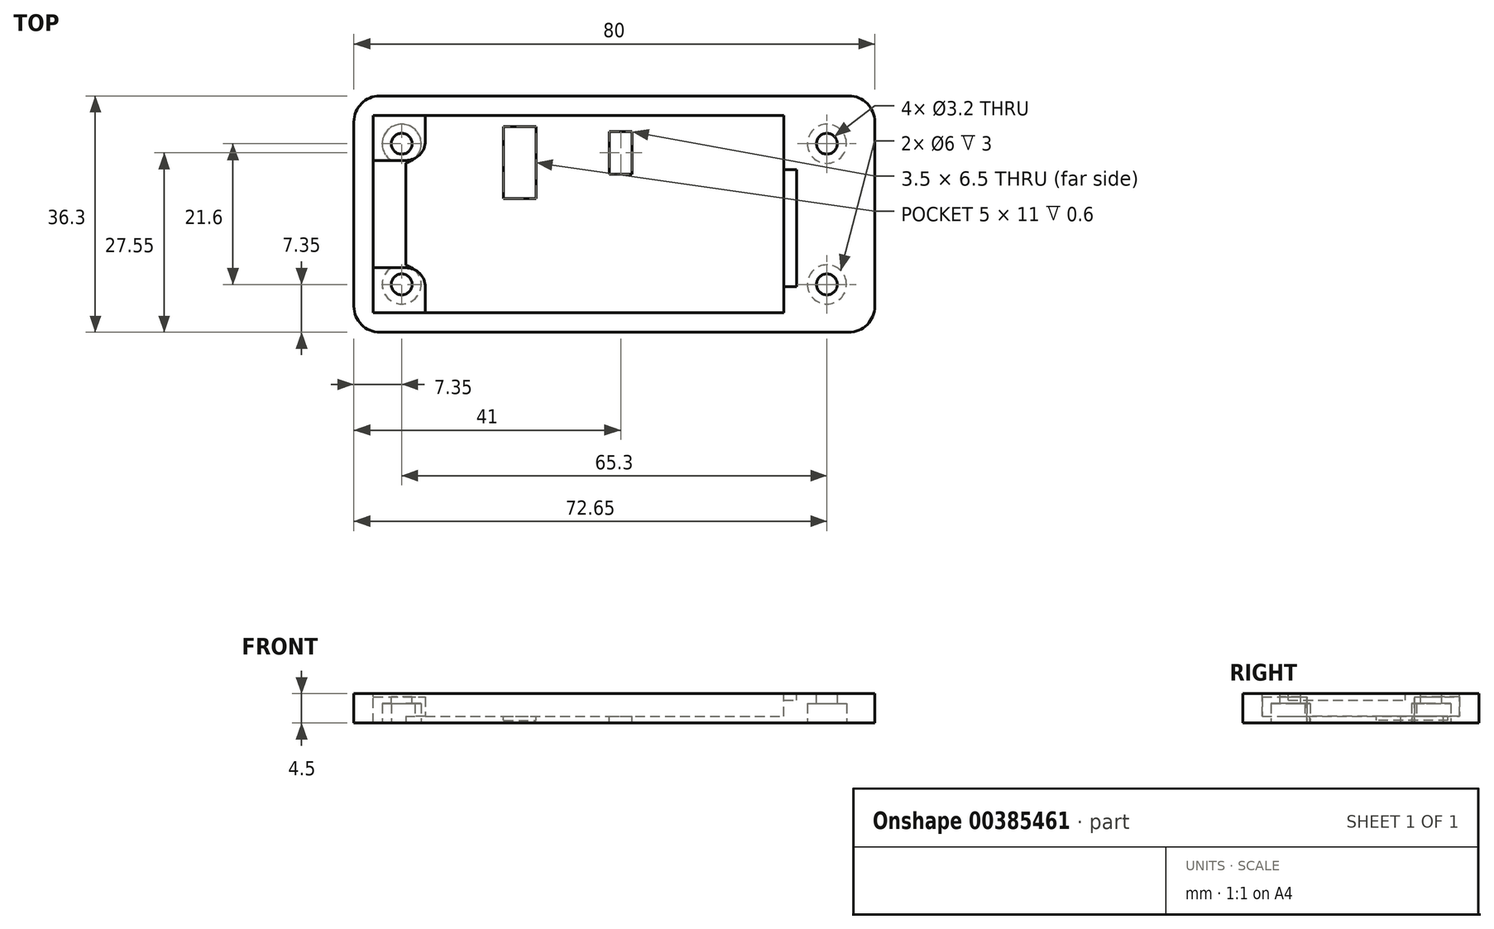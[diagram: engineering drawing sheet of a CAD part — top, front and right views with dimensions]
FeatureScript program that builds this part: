
annotation { "Feature Type Name" : "Feature", "Feature Type Description" : "" }
export const myFeature = defineFeature(function(context is Context, id is Id, definition is map)
    precondition{}
    {
        {
            var Q0;
            Q0=qCreatedBy(makeId("Top.planeOp"),FACE);
            var sketch = newSketch(context, id + "F0", { "sketchPlane" : qUnion([Q0])});
            skLineSegment(sketch, "E0.bottom", {"start": v(0, 0) * mm, "end": v(63, 0) * mm, "construction": true});
            skLineSegment(sketch, "E0.top", {"start": v(0, 30.3) * mm, "end": v(63, 30.3) * mm, "construction": true});
            skLineSegment(sketch, "E0.left", {"start": v(0, 0) * mm, "end": v(0, 30.3) * mm, "construction": true});
            skLineSegment(sketch, "E0.right", {"start": v(63, 0) * mm, "end": v(63, 30.3) * mm, "construction": true});
            skLineSegment(sketch, "E1.0", {"start": v(-3, 33.3) * mm, "end": v(77, 33.3) * mm});
            skLineSegment(sketch, "E1.1", {"start": v(-3, -3) * mm, "end": v(-3, 33.3) * mm});
            skLineSegment(sketch, "E1.2", {"start": v(-3, -3) * mm, "end": v(77, -3) * mm});
            skLineSegment(sketch, "E1.3", {"start": v(77, -3) * mm, "end": v(77, 33.3) * mm});
            skSolve(sketch);
        }
        {
            var Q0;
            Q0=qSketchRegion(id+"F0",true);
            extrude(context, id + "F1", {"entities" : qUnion([Q0]), "depth" : 4.5 * mm});
        }
        {
            var Q0;
            Q0=makeQuery(id+"F1.opExtrude","SWEPT_EDGE",EDGE,{"disambiguationData":[OSD([sQuery(id+"F0.wireOp",EDGE,"E1.1"),sQuery(id+"F0.wireOp",EDGE,"E1.2")])]});
            var Q1;
            Q1=makeQuery(id+"F1.opExtrude","SWEPT_EDGE",EDGE,{"disambiguationData":[OSD([sQuery(id+"F0.wireOp",EDGE,"E1.2"),sQuery(id+"F0.wireOp",EDGE,"E1.3")])]});
            var Q2;
            Q2=makeQuery(id+"F1.opExtrude","SWEPT_EDGE",EDGE,{"disambiguationData":[OSD([sQuery(id+"F0.wireOp",EDGE,"E1.0"),sQuery(id+"F0.wireOp",EDGE,"E1.3")])]});
            var Q3;
            Q3=makeQuery(id+"F1.opExtrude","SWEPT_EDGE",EDGE,{"disambiguationData":[OSD([sQuery(id+"F0.wireOp",EDGE,"E1.0"),sQuery(id+"F0.wireOp",EDGE,"E1.1")])]});
            fillet(context, id + "F2", {"entities" : qUnion([Q0, Q1, Q2, Q3]), "radius" : 4 * mm, "tangentPropagation" : true, "allowEdgeOverflow" : false});
        }
        {
            var Q0;
            Q0=makeQuery(id+"F1.opExtrude","CAP_FACE",FACE,{"disambiguationData":[OSD([sQuery(id+"F0.wireOp",EDGE,"E1.0"),sQuery(id+"F0.wireOp",EDGE,"E1.1"),sQuery(id+"F0.wireOp",EDGE,"E1.2"),sQuery(id+"F0.wireOp",EDGE,"E1.3")])],"isStart":false});
            var sketch = newSketch(context, id + "F3", { "sketchPlane" : qUnion([Q0])});
            skLineSegment(sketch, "E2.bottom", {"start": v(0, 0) * mm, "end": v(63, 0) * mm});
            skLineSegment(sketch, "E2.top", {"start": v(0, 30.3) * mm, "end": v(63, 30.3) * mm});
            skLineSegment(sketch, "E2.left", {"start": v(0, 0) * mm, "end": v(0, 30.3) * mm});
            skLineSegment(sketch, "E2.right", {"start": v(63, 0) * mm, "end": v(63, 30.3) * mm});
            skSolve(sketch);
        }
        {
            var Q0;
            Q0=qSketchRegion(id+"F3",true);
            extrude(context, id + "F4", {"entities" : qUnion([Q0]), "operationType" : NewBodyOperationType.REMOVE, "oppositeDirection" : true, "depth" : 3.5 * mm});
        }
        {
            var Q0;
            Q0=makeQuery(id+"F1.opExtrude","CAP_FACE",FACE,{"disambiguationData":[OSD([sQuery(id+"F0.wireOp",EDGE,"E1.0"),sQuery(id+"F0.wireOp",EDGE,"E1.1"),sQuery(id+"F0.wireOp",EDGE,"E1.2"),sQuery(id+"F0.wireOp",EDGE,"E1.3")])],"isStart":false});
            var sketch = newSketch(context, id + "F5", { "sketchPlane" : qUnion([Q0])});
            skLineSegment(sketch, "E3.bottom", {"start": v(0, 23.4) * mm, "end": v(5, 23.4) * mm});
            skLineSegment(sketch, "E3.top", {"start": v(0, 6.9) * mm, "end": v(5, 6.9) * mm});
            skLineSegment(sketch, "E3.left", {"start": v(0, 23.4) * mm, "end": v(0, 6.9) * mm});
            skLineSegment(sketch, "E3.right", {"start": v(5, 23.4) * mm, "end": v(5, 6.9) * mm});
            skLineSegment(sketch, "E4", {"start": v(0, 15.15) * mm, "end": v(5, 15.15) * mm, "construction": true});
            skLineSegment(sketch, "E5.bottom", {"start": v(36.25, 27.8) * mm, "end": v(39.75, 27.8) * mm});
            skLineSegment(sketch, "E5.top", {"start": v(36.25, 21.3) * mm, "end": v(39.75, 21.3) * mm});
            skLineSegment(sketch, "E5.left", {"start": v(36.25, 27.8) * mm, "end": v(36.25, 21.3) * mm});
            skLineSegment(sketch, "E5.right", {"start": v(39.75, 27.8) * mm, "end": v(39.75, 21.3) * mm});
            skSolve(sketch);
        }
        {
            var Q0;
            Q0=qSketchRegion(id+"F5",true);
            extrude(context, id + "F6", {"entities" : qUnion([Q0]), "operationType" : NewBodyOperationType.REMOVE, "endBound" : BoundingType.THROUGH_ALL, "oppositeDirection" : true, "depth" : 4 * mm});
        }
        {
            var Q0;
            Q0=makeQuery(id+"F1.opExtrude","CAP_FACE",FACE,{"disambiguationData":[OSD([sQuery(id+"F0.wireOp",EDGE,"E1.0"),sQuery(id+"F0.wireOp",EDGE,"E1.1"),sQuery(id+"F0.wireOp",EDGE,"E1.2"),sQuery(id+"F0.wireOp",EDGE,"E1.3")])],"isStart":false});
            var sketch = newSketch(context, id + "F7", { "sketchPlane" : qUnion([Q0])});
            skLineSegment(sketch, "E6.bottom", {"start": v(63, 4) * mm, "end": v(65, 4) * mm});
            skLineSegment(sketch, "E6.top", {"start": v(63, 22) * mm, "end": v(65, 22) * mm});
            skLineSegment(sketch, "E6.left", {"start": v(63, 4) * mm, "end": v(63, 22) * mm});
            skLineSegment(sketch, "E6.right", {"start": v(65, 4) * mm, "end": v(65, 22) * mm});
            skSolve(sketch);
        }
        {
            var Q0;
            Q0=qSketchRegion(id+"F7",true);
            extrude(context, id + "F8", {"entities" : qUnion([Q0]), "operationType" : NewBodyOperationType.REMOVE, "oppositeDirection" : true, "depth" : 1 * mm});
        }
        {
            var Q0;
            Q0=makeQuery(id+"F4.boolean.opBoolean","COPY",FACE,{"derivedFrom":makeQuery(id+"F4.opExtrude","CAP_FACE",FACE,{"disambiguationData":[OSD([sQuery(id+"F3.wireOp",EDGE,"E2.bottom"),sQuery(id+"F3.wireOp",EDGE,"E2.top"),sQuery(id+"F3.wireOp",EDGE,"E2.left"),sQuery(id+"F3.wireOp",EDGE,"E2.right")])],"isStart":false})});
            var sketch = newSketch(context, id + "F9", { "sketchPlane" : qUnion([Q0])});
            skLineSegment(sketch, "E7.bottom", {"start": v(0, 30.3) * mm, "end": v(8, 30.3) * mm});
            skLineSegment(sketch, "E7.top", {"start": v(0, 23.4) * mm, "end": v(5, 23.4) * mm});
            skLineSegment(sketch, "E7.left", {"start": v(0, 30.3) * mm, "end": v(0, 23.4) * mm});
            skLineSegment(sketch, "E7.right", {"start": v(8, 30.3) * mm, "end": v(8, 26.4) * mm});
            skLineSegment(sketch, "E8", {"start": v(0, 15.15) * mm, "end": v(66.77, 15.15) * mm, "construction": true});
            skLineSegment(sketch, "E9.MirrorCS", {"start": v(0, 6.9) * mm, "end": v(5, 6.9) * mm});
            skLineSegment(sketch, "E10.MirrorCS", {"start": v(8, 0) * mm, "end": v(8, 3.9) * mm});
            skLineSegment(sketch, "E11.MirrorCS", {"start": v(0, 0) * mm, "end": v(8, 0) * mm});
            skLineSegment(sketch, "E12.MirrorCS", {"start": v(0, 0) * mm, "end": v(0, 6.9) * mm});
            skPoint(sketch, "E13.visualSharp", {"position": v(8, 23.4) * mm});
            skArc(sketch, "E13.filletArc", {"start": v(5, 23.4) * mm, "mid": v(7.12, 24.28) * mm, "end": v(8, 26.4) * mm});
            skPoint(sketch, "E14.visualSharp", {"position": v(8, 6.9) * mm});
            skArc(sketch, "E14.filletArc", {"start": v(8, 3.9) * mm, "mid": v(7.12, 6.02) * mm, "end": v(5, 6.9) * mm});
            skSolve(sketch);
        }
        {
            var Q0;
            Q0 = qSketchRegion(id + "F9", true);
            extrude(context, id + "F10", {"entities" : qUnion([Q0]), "operationType" : NewBodyOperationType.ADD, "depth" : 3 * mm});
        }
        {
            var Q0;
            Q0=makeQuery(id+"F1.opExtrude","CAP_FACE",FACE,{"disambiguationData":[OSD([sQuery(id+"F0.wireOp",EDGE,"E1.0"),sQuery(id+"F0.wireOp",EDGE,"E1.1"),sQuery(id+"F0.wireOp",EDGE,"E1.2"),sQuery(id+"F0.wireOp",EDGE,"E1.3")])],"isStart":false});
            var sketch = newSketch(context, id + "F11", { "sketchPlane" : qUnion([Q0])});
            skCircle(sketch, "E15", {"center": v(4.35, 4.35) * mm, "radius": 1.6 * mm});
            skCircle(sketch, "E16", {"center": v(4.35, 25.95) * mm, "radius": 1.6 * mm});
            skLineSegment(sketch, "E17", {"start": v(4.35, 25.95) * mm, "end": v(4.35, 4.35) * mm, "construction": true});
            skLineSegment(sketch, "E18", {"start": v(0, 15.15) * mm, "end": v(4.35, 15.15) * mm, "construction": true});
            skCircle(sketch, "E19.1.0.0", {"center": v(69.65, 25.95) * mm, "radius": 1.6 * mm});
            skCircle(sketch, "E19.1.0.1", {"center": v(69.65, 4.35) * mm, "radius": 1.6 * mm});
            skLineSegment(sketch, "E19.direction1", {"start": v(4.35, 4.35) * mm, "end": v(69.65, 4.35) * mm, "construction": true});
            skSolve(sketch);
        }
        {
            var Q0;
            Q0=qSketchRegion(id+"F11",true);
            extrude(context, id + "F12", {"entities" : qUnion([Q0]), "operationType" : NewBodyOperationType.REMOVE, "endBound" : BoundingType.THROUGH_ALL, "oppositeDirection" : true, "depth" : 25 * mm});
        }
        {
            var Q0;
            Q0=makeQuery(id+"F1.opExtrude","CAP_FACE",FACE,{"disambiguationData":[OSD([sQuery(id+"F0.wireOp",EDGE,"E1.0"),sQuery(id+"F0.wireOp",EDGE,"E1.1"),sQuery(id+"F0.wireOp",EDGE,"E1.2"),sQuery(id+"F0.wireOp",EDGE,"E1.3")])],"isStart":true});
            var sketch = newSketch(context, id + "F13", { "sketchPlane" : qUnion([Q0])});
            skCircle(sketch, "E20.cCircle", {"center": v(69.65, -25.95) * mm, "radius": 3 * mm});
            skPoint(sketch, "E20.0.midPoint", {"position": v(69.65, -28.95) * mm});
            skPoint(sketch, "E21.0.1.3", {"position": v(69.65, -7.35) * mm});
            skCircle(sketch, "E21.0.1.4", {"center": v(69.65, -4.35) * mm, "radius": 3 * mm});
            skPoint(sketch, "E21.1.0.3", {"position": v(4.35, -28.95) * mm});
            skCircle(sketch, "E21.1.0.4", {"center": v(4.35, -25.95) * mm, "radius": 3 * mm});
            skLineSegment(sketch, "E21.1.0.7", {"start": v(6.08, -28.95) * mm, "end": v(2.62, -28.95) * mm});
            skPoint(sketch, "E21.1.1.3", {"position": v(4.35, -7.35) * mm});
            skCircle(sketch, "E21.1.1.4", {"center": v(4.35, -4.35) * mm, "radius": 3 * mm});
            skLineSegment(sketch, "E21.direction1", {"start": v(67.92, -28.95) * mm, "end": v(2.62, -28.95) * mm, "construction": true});
            skLineSegment(sketch, "E21.direction2", {"start": v(67.92, -28.95) * mm, "end": v(67.92, -7.35) * mm, "construction": true});
            skSolve(sketch);
        }
        {
            var Q0;
            Q0=qSketchRegion(id+"F13",true);
            extrude(context, id + "F14", {"entities" : qUnion([Q0]), "operationType" : NewBodyOperationType.REMOVE, "oppositeDirection" : true, "depth" : 3 * mm});
        }
        {
            var Q0;
            Q0=makeQuery(id+"F4.boolean.opBoolean","COPY",FACE,{"derivedFrom":makeQuery(id+"F4.opExtrude","CAP_FACE",FACE,{"disambiguationData":[OSD([sQuery(id+"F3.wireOp",EDGE,"E2.bottom"),sQuery(id+"F3.wireOp",EDGE,"E2.top"),sQuery(id+"F3.wireOp",EDGE,"E2.left"),sQuery(id+"F3.wireOp",EDGE,"E2.right")])],"isStart":false})});
            var sketch = newSketch(context, id + "F15", { "sketchPlane" : qUnion([Q0])});
            skLineSegment(sketch, "E22.bottom", {"start": v(20, 28.55) * mm, "end": v(25, 28.55) * mm});
            skLineSegment(sketch, "E22.top", {"start": v(20, 17.55) * mm, "end": v(25, 17.55) * mm});
            skLineSegment(sketch, "E22.left", {"start": v(20, 28.55) * mm, "end": v(20, 17.55) * mm});
            skLineSegment(sketch, "E22.right", {"start": v(25, 28.55) * mm, "end": v(25, 17.55) * mm});
            skSolve(sketch);
        }
        {
            var Q0;
            Q0 = qSketchRegion(id + "F15", true);
            extrude(context, id + "F16", {"entities" : qUnion([Q0]), "operationType" : NewBodyOperationType.REMOVE, "oppositeDirection" : true, "depth" : 0.6 * mm});
        }
    });
